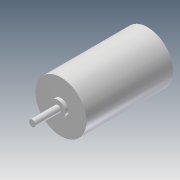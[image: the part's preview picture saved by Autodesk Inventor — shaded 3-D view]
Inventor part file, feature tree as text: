
AUTODESK INVENTOR PART (.ipt)
format: ipt  version: 2014 (Build 180170000, 170)  size: 89,088 bytes
history: native  units: in
note: dims shown in document units (in); Inventor stores cm internally (conversion verified against a paired STEP export)
features: extrude x3, sketch x3
ambient origin geometry x8: Origin, YZ Plane, XZ Plane, XY Plane, X Axis, Y Axis, Z Axis, Center Point
bodies: Solid1 (feature_tree)
feature tree (6):
  extrude  "Extrusion1"  Depth=4.25in TaperAngle=0.0deg
  extrude  "Extrusion2"  Depth=0.15in TaperAngle=0.0deg
  extrude  "Extrusion3"  Depth=1.25in TaperAngle=0.0deg
  sketch  "Sketch1"  dims[d0=2.5in d1=4.25in d2=0.0in]
  sketch  "Sketch2"  dims[d3=0.75in d4=0.15in d5=0.0in]
  sketch  "Sketch3"  dims[d6=0.3125in d7=1.25in d8=0.0in]
